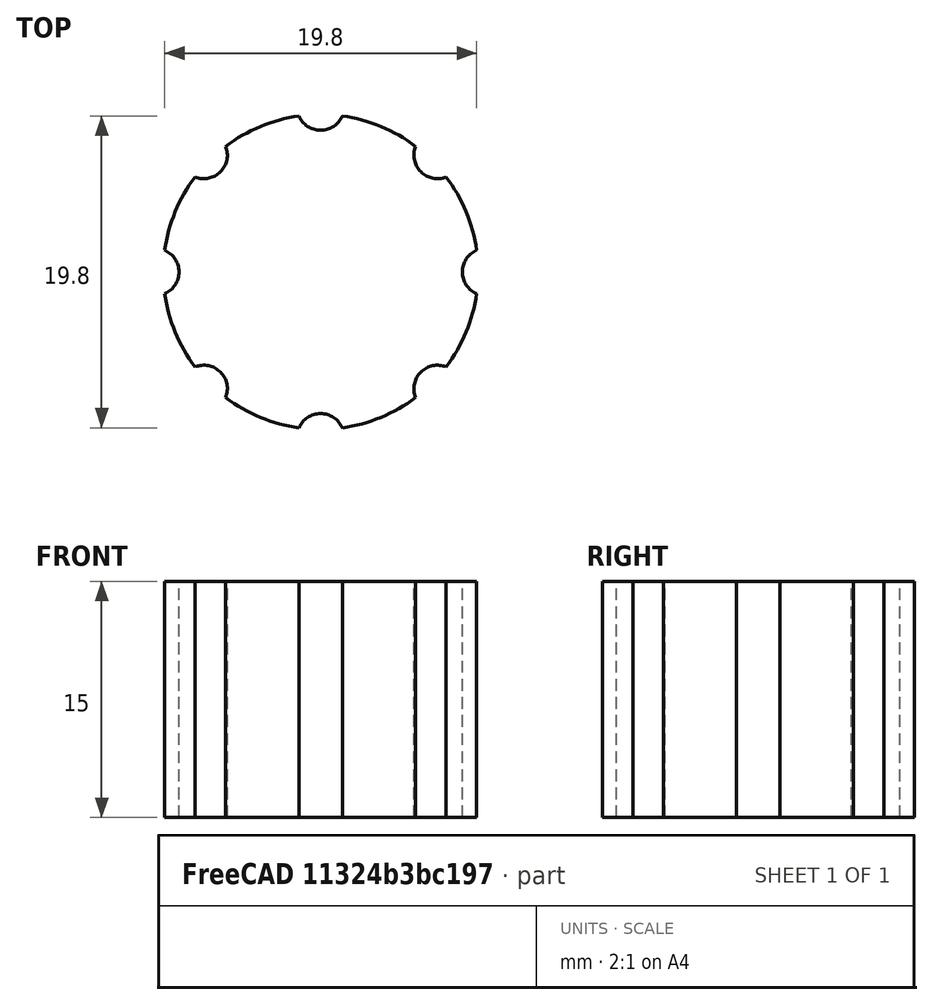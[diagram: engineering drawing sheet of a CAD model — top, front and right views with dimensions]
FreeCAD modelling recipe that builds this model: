
FCSTD DOCUMENT  (FreeCAD 0.18.4R)
Label: tutorial_freecad_ex11_b
License: All rights reserved
LicenseURL: http://en.wikipedia.org/wiki/All_rights_reserved
objects: Part::Cylinder×2, Part::FeaturePython×1, Part::Cut×1
note: 4 computed .brp shape members not serialized (recipe doc carries the construction recipe); baked Part::Feature solids carry a one-line shape summary decoded from their .brp

FEATURE [Part::Cylinder] Cylinder  label="base"
  Angle = 360
  AttacherType = Attacher::AttachEngine3D
  Height = 15
  Radius = 10
FEATURE [Part::Cylinder] Cylinder001  label="muesca_master"
  Angle = 360
  AttacherType = Attacher::AttachEngine3D
  Height = 19
  Placement = pos=(10.5,0,-2) rot=(0,0,1;0rad)
  Radius = 1.5
FEATURE [Part::FeaturePython] Array  label="muescas"  # Draft array (typed FeaturePython)
  Angle = 360
  ArrayType = 1
  Axis = (0,0,1)
  Base = -> Cylinder001
  Center = (0,0,0)
  Fuse = false
  IntervalAxis = (0,0,0)
  IntervalX = (1,0,0)
  IntervalY = (0,1,0)
  IntervalZ = (0,0,1)
  NumberPolar = 8
  NumberX = 2
  NumberY = 2
  NumberZ = 1
FEATURE [Part::Cut] Cut
  Base = -> Cylinder
  Refine = true
  Tool = -> Array
